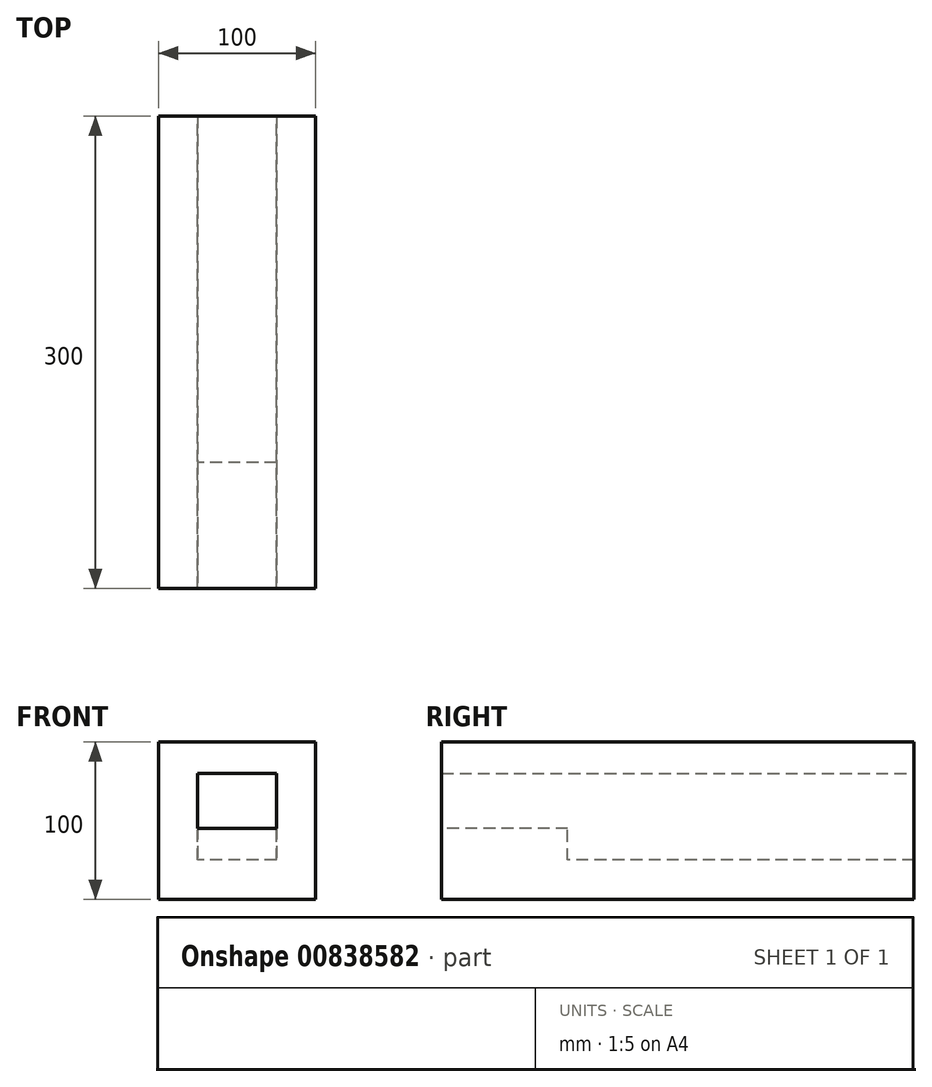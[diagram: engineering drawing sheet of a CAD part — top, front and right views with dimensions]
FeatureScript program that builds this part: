
annotation { "Feature Type Name" : "Feature", "Feature Type Description" : "" }
export const myFeature = defineFeature(function(context is Context, id is Id, definition is map)
    precondition{}
    {
        {
            var Q0;
            Q0=qCreatedBy(makeId("Right.planeOp"),FACE);
            var sketch = newSketch(context, id + "F0", { "sketchPlane" : qUnion([Q0])});
            skLineSegment(sketch, "E0.bottom", {"start": v(-150, 50) * mm, "end": v(150, 50) * mm});
            skLineSegment(sketch, "E0.top", {"start": v(-150, -50) * mm, "end": v(150, -50) * mm});
            skLineSegment(sketch, "E0.left", {"start": v(-150, 50) * mm, "end": v(-150, -50) * mm});
            skLineSegment(sketch, "E0.right", {"start": v(150, 50) * mm, "end": v(150, -50) * mm});
            skSolve(sketch);
        }
        {
            var Q0;
            Q0 = qSketchRegion(id + "F0", true);
            extrude(context, id + "F1", {"entities" : qUnion([Q0]), "depth" : 100 * mm, "offsetDistance" : 25 * mm, "symmetric" : true});
        }
        {
            var Q0;
            Q0=qCreatedBy(makeId("Right.planeOp"),FACE);
            var sketch = newSketch(context, id + "F2", { "sketchPlane" : qUnion([Q0])});
            skLineSegment(sketch, "E1.0", {"start": v(-150, 50) * mm, "end": v(-150, -50) * mm, "construction": true});
            skLineSegment(sketch, "E1.1", {"start": v(150, 50) * mm, "end": v(150, -50) * mm, "construction": true});
            skLineSegment(sketch, "E2", {"start": v(-150, 30) * mm, "end": v(150, 30) * mm});
            skLineSegment(sketch, "E3", {"start": v(150, 30) * mm, "end": v(150, -25) * mm});
            skLineSegment(sketch, "E4", {"start": v(150, -25) * mm, "end": v(-70, -25) * mm});
            skLineSegment(sketch, "E5", {"start": v(-70, -25) * mm, "end": v(-70, -5) * mm});
            skLineSegment(sketch, "E6", {"start": v(-70, -5) * mm, "end": v(-150, -5) * mm});
            skLineSegment(sketch, "E7", {"start": v(-150, -5) * mm, "end": v(-150, 30) * mm});
            skSolve(sketch);
        }
        {
            var Q0;
            Q0 = qSketchRegion(id + "F2", true);
            extrude(context, id + "F3", {"entities" : qUnion([Q0]), "depth" : 50 * mm, "offsetDistance" : 25 * mm, "symmetric" : true});
        }
        {
            var Q0;
            Q0=makeQuery(id+"F3.opExtrude","SWEPT_BODY",BODY,{"disambiguationData":[OSD([sQuery(id+"F2.wireOp",EDGE,"E2"),sQuery(id+"F2.wireOp",EDGE,"E3"),sQuery(id+"F2.wireOp",EDGE,"E4"),sQuery(id+"F2.wireOp",EDGE,"E5"),sQuery(id+"F2.wireOp",EDGE,"E6"),sQuery(id+"F2.wireOp",EDGE,"E7")])]});
            var Q1;
            Q1=makeQuery(id+"F1.opExtrude","SWEPT_BODY",BODY,{"disambiguationData":[OSD([sQuery(id+"F0.wireOp",EDGE,"E0.bottom"),sQuery(id+"F0.wireOp",EDGE,"E0.top"),sQuery(id+"F0.wireOp",EDGE,"E0.left"),sQuery(id+"F0.wireOp",EDGE,"E0.right")])]});
            booleanBodies(context, id + "F4", {"operationType" : BooleanOperationType.SUBTRACTION, "tools" : qUnion([Q0]), "targets" : qUnion([Q1]), "keepTools" : true});
        }
    });
